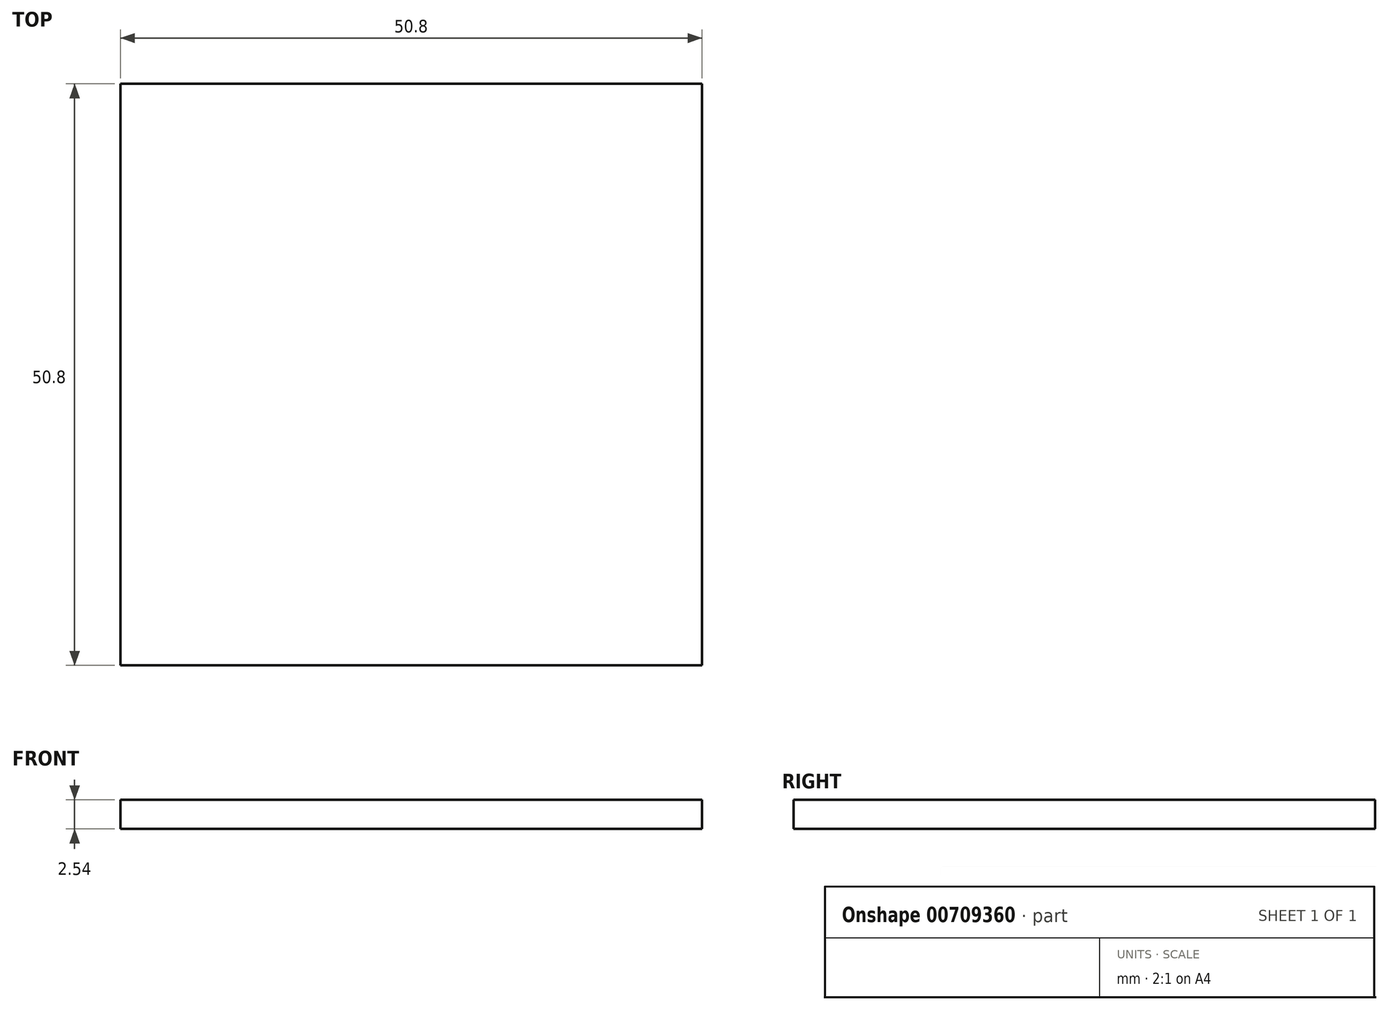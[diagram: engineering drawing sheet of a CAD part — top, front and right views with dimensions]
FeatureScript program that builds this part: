
annotation { "Feature Type Name" : "Feature", "Feature Type Description" : "" }
export const myFeature = defineFeature(function(context is Context, id is Id, definition is map)
    precondition{}
    {
        {
            var Q0;
            Q0=qCreatedBy(makeId("Top.planeOp"),FACE);
            var sketch = newSketch(context, id + "F0", { "sketchPlane" : qUnion([Q0])});
            skLineSegment(sketch, "E0.bottom", {"start": v(-25.4, 25.4) * mm, "end": v(25.4, 25.4) * mm});
            skLineSegment(sketch, "E0.top", {"start": v(-25.4, -25.4) * mm, "end": v(25.4, -25.4) * mm});
            skLineSegment(sketch, "E0.left", {"start": v(-25.4, 25.4) * mm, "end": v(-25.4, -25.4) * mm});
            skLineSegment(sketch, "E0.right", {"start": v(25.4, 25.4) * mm, "end": v(25.4, -25.4) * mm});
            skPoint(sketch, "E0.middle", {"position": v(0, 0) * mm});
            skSolve(sketch);
        }
        {
            var Q0;
            Q0=makeQuery(id+"F0.imprint","IMPRINT",FACE,{"disambiguationData":[TD([[makeQuery(id+"F0.imprint","IMPRINT",EDGE,{"derivedFrom":sQuery(id+"F0.wireOp",EDGE,"E0.bottom")}),-1.0]])]});
            extrude(context, id + "F1", {"entities" : qUnion([Q0]), "depth" : 2.54 * mm, "offsetDistance" : 25.4 * mm});
        }
    });
